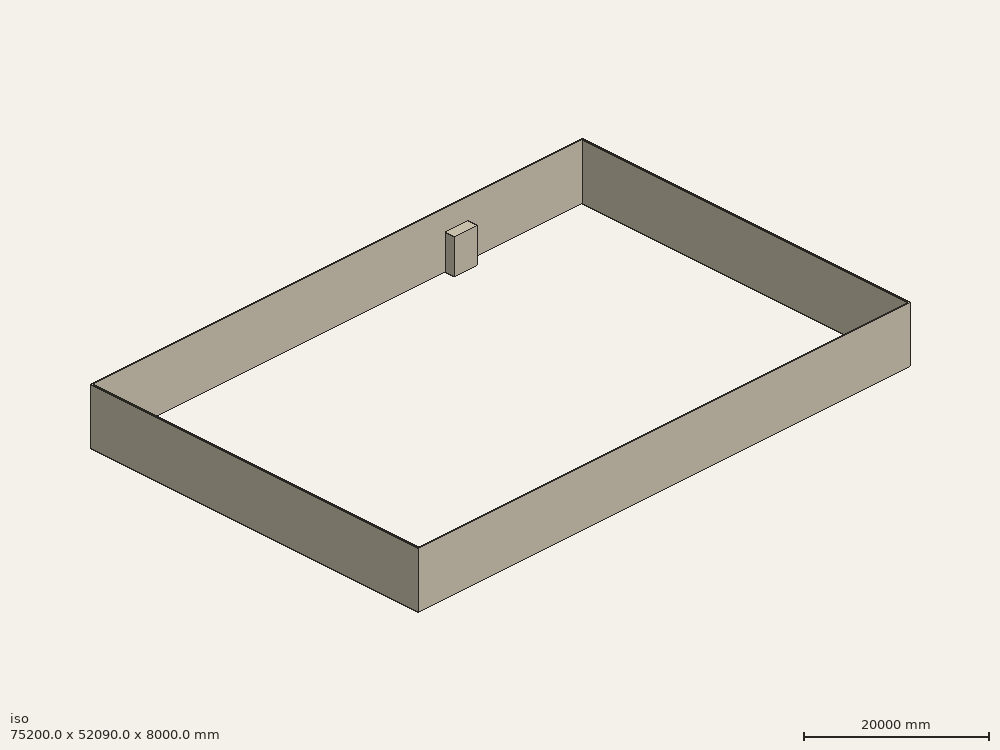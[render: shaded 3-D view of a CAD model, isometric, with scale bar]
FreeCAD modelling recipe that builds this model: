
FCSTD DOCUMENT  (FreeCAD 0.19R)
Label: factory
License: All rights reserved
LicenseURL: http://en.wikipedia.org/wiki/All_rights_reserved
objects: Part::Part2DObjectPython×1, Part::Box×1, Part::FeaturePython×1
note: 3 computed .brp shape members not serialized (recipe doc carries the construction recipe); baked Part::Feature solids carry a one-line shape summary decoded from their .brp

FEATURE [Part::Part2DObjectPython] Rectangle  # Draft 2D object (typed FeaturePython)
  Area = 0
  ChamferSize = 0
  Columns = 1
  FilletRadius = 0
  Height = 50000
  Length = 75000
  MakeFace = false
  Placement = pos=(-30000,-38000,0) rot=(0,0,1;0rad)
  Rows = 1
FEATURE [Part::Box] Cube
  AttacherType = Attacher::AttachEngine3D
  Height = 5000
  Length = 3500
  Placement = pos=(23990,13990,5000) rot=(0.999977,-0.006849,0;3.14159rad)
  Width = 3500
FEATURE [Part::FeaturePython] Wall  # Arch/BIM 166 (typed FeaturePython)
  Align = 2
  Area = 2000000000
  Base = -> Rectangle
  BlockHeight = 0
  BlockLength = 0
  CountBroken = 0
  CountEntire = 0
  Face = 0
  Height = 8000
  HorizontalArea = 50000000
  IfcData = attributes={"GlobalId": {"name": "GlobalId", "type": "IfcGloballyUniqueId", "is_enum": false, "enum_values": []}, "Description": {"... (+533 chars omitted),+1 more (map truncated)
  IfcType = 166
  Joint = 0
  Length = 250000
  MakeBlocks = false
  MoveBase = false
  MoveWithHost = false
  Normal = (0,0,0)
  OffsetFirst = 0
  OffsetSecond = 0
  PerimeterLength = 250800
  PredefinedType = 0
  Subtractions = -> [Cube]
  VerticalArea = 3.967e+09
  Width = 200
